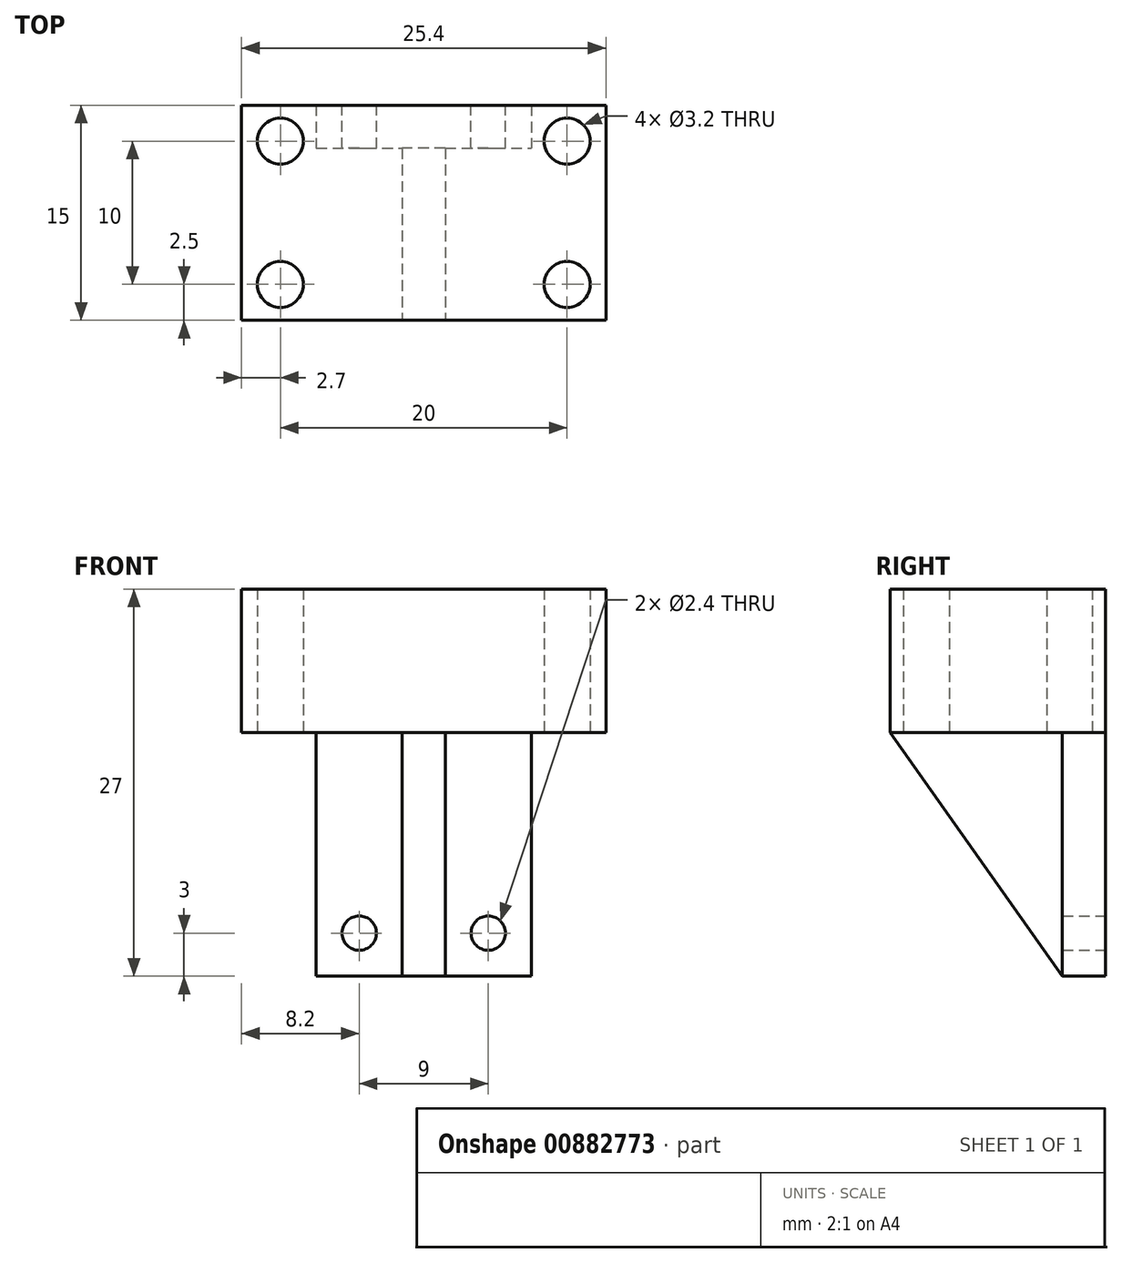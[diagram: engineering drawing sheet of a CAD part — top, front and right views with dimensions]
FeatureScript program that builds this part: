
annotation { "Feature Type Name" : "Feature", "Feature Type Description" : "" }
export const myFeature = defineFeature(function(context is Context, id is Id, definition is map)
    precondition{}
    {
        {
            var Q0;
            Q0=qCreatedBy(makeId("Top.planeOp"),FACE);
            var sketch = newSketch(context, id + "F0", { "sketchPlane" : qUnion([Q0])});
            skLineSegment(sketch, "E0.bottom", {"start": v(12.7, -7.5) * mm, "end": v(-12.7, -7.5) * mm});
            skLineSegment(sketch, "E0.top", {"start": v(12.7, 7.5) * mm, "end": v(-12.7, 7.5) * mm});
            skLineSegment(sketch, "E0.left", {"start": v(12.7, -7.5) * mm, "end": v(12.7, 7.5) * mm});
            skLineSegment(sketch, "E0.right", {"start": v(-12.7, -7.5) * mm, "end": v(-12.7, 7.5) * mm});
            skPoint(sketch, "E0.middle", {"position": v(0, 0) * mm});
            skSolve(sketch);
        }
        {
            var Q0;
            Q0 = qSketchRegion(id + "F0", true);
            extrude(context, id + "F1", {"entities" : qUnion([Q0]), "depth" : 10 * mm, "offsetDistance" : 25.4 * mm});
        }
        {
            var Q0;
            Q0=makeQuery(id+"F1.opExtrude","CAP_FACE",FACE,{"disambiguationData":[OSD([sQuery(id+"F0.wireOp",EDGE,"E0.bottom"),sQuery(id+"F0.wireOp",EDGE,"E0.top"),sQuery(id+"F0.wireOp",EDGE,"E0.left"),sQuery(id+"F0.wireOp",EDGE,"E0.right")])],"isStart":true});
            var sketch = newSketch(context, id + "F2", { "sketchPlane" : qUnion([Q0])});
            skCircle(sketch, "E1", {"center": v(-10, 5) * mm, "radius": 1.6 * mm});
            skCircle(sketch, "E2", {"center": v(-10, -5) * mm, "radius": 1.6 * mm});
            skLineSegment(sketch, "E3", {"start": v(-12.7, 0) * mm, "end": v(12.7, 0) * mm});
            skLineSegment(sketch, "E4", {"start": v(0, 7.5) * mm, "end": v(0, -7.5) * mm});
            skCircle(sketch, "E5.MirrorC", {"center": v(10, -5) * mm, "radius": 1.6 * mm});
            skCircle(sketch, "E6.MirrorC", {"center": v(10, 5) * mm, "radius": 1.6 * mm});
            skSolve(sketch);
        }
        {
            var Q0;
            Q0 = qSketchRegion(id + "F2", true);
            extrude(context, id + "F3", {"entities" : qUnion([Q0]), "operationType" : NewBodyOperationType.REMOVE, "endBound" : BoundingType.UP_TO_NEXT, "oppositeDirection" : true, "depth" : 25.4 * mm, "offsetDistance" : 25.4 * mm});
        }
        {
            var Q0;
            Q0=makeQuery(id+"F1.opExtrude","CAP_FACE",FACE,{"disambiguationData":[OSD([sQuery(id+"F0.wireOp",EDGE,"E0.bottom"),sQuery(id+"F0.wireOp",EDGE,"E0.top"),sQuery(id+"F0.wireOp",EDGE,"E0.left"),sQuery(id+"F0.wireOp",EDGE,"E0.right")])],"isStart":true});
            var sketch = newSketch(context, id + "F4", { "sketchPlane" : qUnion([Q0])});
            skLineSegment(sketch, "E7.bottom", {"start": v(-7.5, -7.5) * mm, "end": v(7.5, -7.5) * mm});
            skLineSegment(sketch, "E7.top", {"start": v(-7.5, -4.5) * mm, "end": v(-1.5, -4.5) * mm});
            skLineSegment(sketch, "E7.left", {"start": v(-7.5, -7.5) * mm, "end": v(-7.5, -4.5) * mm});
            skLineSegment(sketch, "E7.right", {"start": v(7.5, -7.5) * mm, "end": v(7.5, -4.5) * mm});
            skLineSegment(sketch, "E8.top", {"start": v(-1.5, 7.5) * mm, "end": v(1.5, 7.5) * mm});
            skLineSegment(sketch, "E8.left", {"start": v(-1.5, -4.5) * mm, "end": v(-1.5, 7.5) * mm});
            skLineSegment(sketch, "E8.right", {"start": v(1.5, -4.5) * mm, "end": v(1.5, 7.5) * mm});
            skLineSegment(sketch, "E9", {"start": v(0, 7.5) * mm, "end": v(0, -7.5) * mm});
            skLineSegment(sketch, "E10.trimOffspring", {"start": v(1.5, -4.5) * mm, "end": v(7.5, -4.5) * mm});
            skSolve(sketch);
        }
        {
            var Q0;
            Q0 = qSketchRegion(id + "F4", true);
            extrude(context, id + "F5", {"entities" : qUnion([Q0]), "operationType" : NewBodyOperationType.ADD, "depth" : 17 * mm, "offsetDistance" : 25.4 * mm});
        }
        {
            var Q0;
            Q0=makeQuery(id+"F5.opExtrude","SWEPT_FACE",FACE,{"disambiguationData":[OSD([sQuery(id+"F4.wireOp",EDGE,"E8.left")])]});
            var sketch = newSketch(context, id + "F6", { "sketchPlane" : qUnion([Q0])});
            skLineSegment(sketch, "E11", {"start": v(7.5, 0) * mm, "end": v(-4.5, -17) * mm});
            skLineSegment(sketch, "E12", {"start": v(-4.5, -17) * mm, "end": v(7.5, -17) * mm});
            skLineSegment(sketch, "E13", {"start": v(7.5, -17) * mm, "end": v(7.5, 0) * mm});
            skSolve(sketch);
        }
        {
            var Q0;
            Q0 = qSketchRegion(id + "F6", true);
            extrude(context, id + "F7", {"entities" : qUnion([Q0]), "operationType" : NewBodyOperationType.REMOVE, "endBound" : BoundingType.UP_TO_NEXT, "oppositeDirection" : true, "depth" : 25.4 * mm, "offsetDistance" : 25.4 * mm});
        }
        {
            var Q0;
            Q0=makeQuery(id+"F5.boolean.opBoolean","MERGE",FACE,{"derivedFrom":[makeQuery(id+"F1.opExtrude","SWEPT_FACE",FACE,{"disambiguationData":[OSD([sQuery(id+"F0.wireOp",EDGE,"E0.top")])]}),makeQuery(id+"F5.opExtrude","SWEPT_FACE",FACE,{"disambiguationData":[OSD([sQuery(id+"F4.wireOp",EDGE,"E7.bottom")])]})]});
            var sketch = newSketch(context, id + "F8", { "sketchPlane" : qUnion([Q0])});
            skCircle(sketch, "E14", {"center": v(-4.5, -14) * mm, "radius": 1.2 * mm});
            skCircle(sketch, "E15.MirrorC", {"center": v(4.5, -14) * mm, "radius": 1.2 * mm});
            skSolve(sketch);
        }
        {
            var Q0;
            Q0 = qSketchRegion(id + "F8", true);
            extrude(context, id + "F9", {"entities" : qUnion([Q0]), "operationType" : NewBodyOperationType.REMOVE, "endBound" : BoundingType.UP_TO_NEXT, "oppositeDirection" : true, "depth" : 25.4 * mm, "offsetDistance" : 25.4 * mm});
        }
    });
